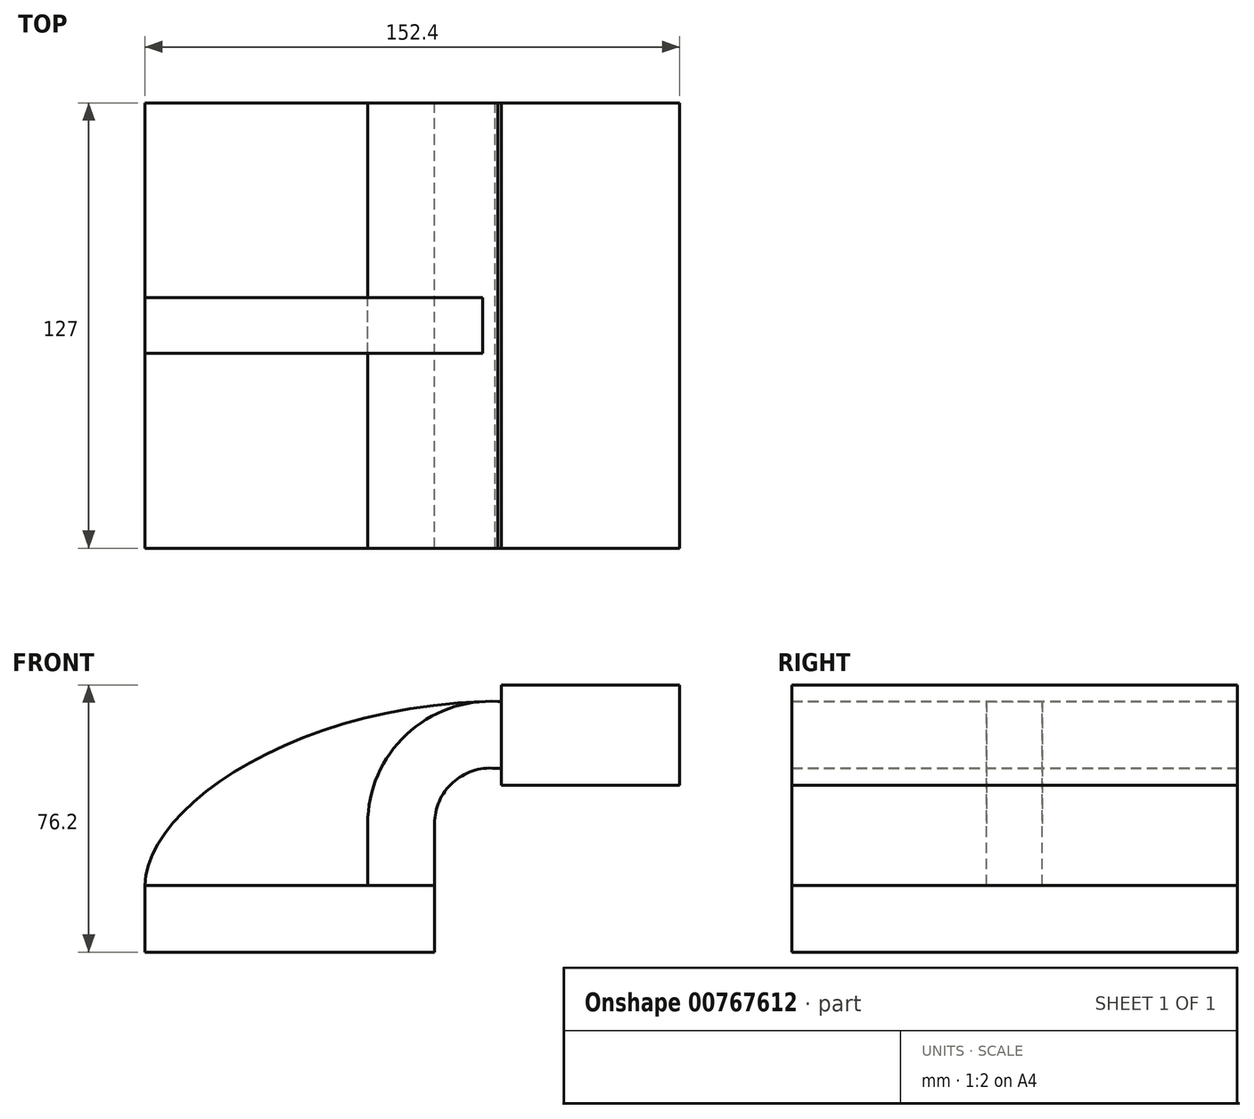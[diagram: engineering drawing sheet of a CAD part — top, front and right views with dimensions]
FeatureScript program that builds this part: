
annotation { "Feature Type Name" : "Feature", "Feature Type Description" : "" }
export const myFeature = defineFeature(function(context is Context, id is Id, definition is map)
    precondition{}
    {
        {
            var Q0;
            Q0=qCreatedBy(makeId("Front.planeOp"),FACE);
            var sketch = newSketch(context, id + "F0", { "sketchPlane" : qUnion([Q0])});
            skLineSegment(sketch, "E0.bottom", {"start": v(41.27, 9.53) * mm, "end": v(-41.28, 9.53) * mm});
            skLineSegment(sketch, "E0.top", {"start": v(41.28, -9.52) * mm, "end": v(-41.27, -9.52) * mm});
            skLineSegment(sketch, "E0.left", {"start": v(41.28, 9.53) * mm, "end": v(41.28, -9.52) * mm});
            skLineSegment(sketch, "E0.right", {"start": v(-41.28, 9.53) * mm, "end": v(-41.28, -9.52) * mm});
            skPoint(sketch, "E0.middle", {"position": v(0, 0) * mm});
            skLineSegment(sketch, "E1.bottom", {"start": v(111.12, 66.68) * mm, "end": v(60.32, 66.68) * mm});
            skLineSegment(sketch, "E1.top", {"start": v(111.12, 38.1) * mm, "end": v(60.32, 38.1) * mm});
            skLineSegment(sketch, "E1.left", {"start": v(111.12, 66.68) * mm, "end": v(111.12, 38.1) * mm});
            skLineSegment(sketch, "E1.right", {"start": v(60.32, 66.68) * mm, "end": v(60.32, 38.1) * mm});
            skPoint(sketch, "E1.middle", {"position": v(85.72, 52.39) * mm});
            skLineSegment(sketch, "E2", {"start": v(41.27, 9.53) * mm, "end": v(41.27, 27.07) * mm});
            skArc(sketch, "E3", {"start": v(41.27, 27.07) * mm, "mid": v(46.45, 38.79) * mm, "end": v(58.6, 42.88) * mm});
            skLineSegment(sketch, "E4", {"start": v(58.6, 42.88) * mm, "end": v(85.97, 42.88) * mm});
            skLineSegment(sketch, "E5.0", {"start": v(59.29, 61.93) * mm, "end": v(85.97, 61.93) * mm});
            skArc(sketch, "E5.1", {"start": v(22.22, 27.07) * mm, "mid": v(33.22, 52.5) * mm, "end": v(59.29, 61.93) * mm});
            skLineSegment(sketch, "E5.2", {"start": v(22.22, 9.53) * mm, "end": v(22.22, 27.07) * mm});
            skFitSpline(sketch, "E6", {"points": [v(-41.28, 9.53) * mm, v(55.01, 61.93) * mm], "startDerivative": vector(0.67, 65.22) * mm, "endDerivative": vector(165.04, 5.92) * mm});
            skSolve(sketch);
        }
        {
            var Q0;
            Q0=makeQuery(id+"F0.imprint","IMPRINT",FACE,{"disambiguationData":[TD([[makeQuery(id+"F0.imprint","IMPRINT",EDGE,{"derivedFrom":sQuery(id+"F0.wireOp",EDGE,"E0.top")}),-1.0]])]});
            extrude(context, id + "F1", {"entities" : qUnion([Q0]), "endBound" : BoundingType.SYMMETRIC, "depth" : 127 * mm, "offsetDistance" : 25.4 * mm});
        }
        {
            var Q0;
            {var subQ1=sQuery(id+"F0.wireOp",EDGE,"E1.bottom");Q0=makeQuery(id+"F0.imprint","IMPRINT",FACE,{"disambiguationData":[TD([[makeQuery(id+"F0.imprint","IMPRINT",EDGE,{"derivedFrom":subQ1}),1.0]])]});}
            extrude(context, id + "F2", {"entities" : qUnion([Q0]), "endBound" : BoundingType.SYMMETRIC, "depth" : 127 * mm, "offsetDistance" : 25.4 * mm});
        }
        {
            var Q0;
            {var subQ1=sQuery(id+"F0.wireOp",EDGE,"E2");Q0=makeQuery(id+"F0.imprint","IMPRINT",FACE,{"disambiguationData":[TD([[makeQuery(id+"F0.imprint","IMPRINT",EDGE,{"derivedFrom":subQ1}),1.0]])]});}
            extrude(context, id + "F3", {"entities" : qUnion([Q0]), "endBound" : BoundingType.SYMMETRIC, "depth" : 127 * mm, "offsetDistance" : 25.4 * mm});
        }
        {
            var Q0;
            {var subQ2=sQuery(id+"F0.wireOp",EDGE,"E5.2");Q0=makeQuery(id+"F0.imprint","IMPRINT",FACE,{"disambiguationData":[TD([[makeQuery(id+"F0.imprint","IMPRINT",EDGE,{"derivedFrom":subQ2}),1.0]])]});}
            extrude(context, id + "F4", {"entities" : qUnion([Q0]), "endBound" : BoundingType.SYMMETRIC, "depth" : 15.88 * mm, "offsetDistance" : 25.4 * mm});
        }
    });
